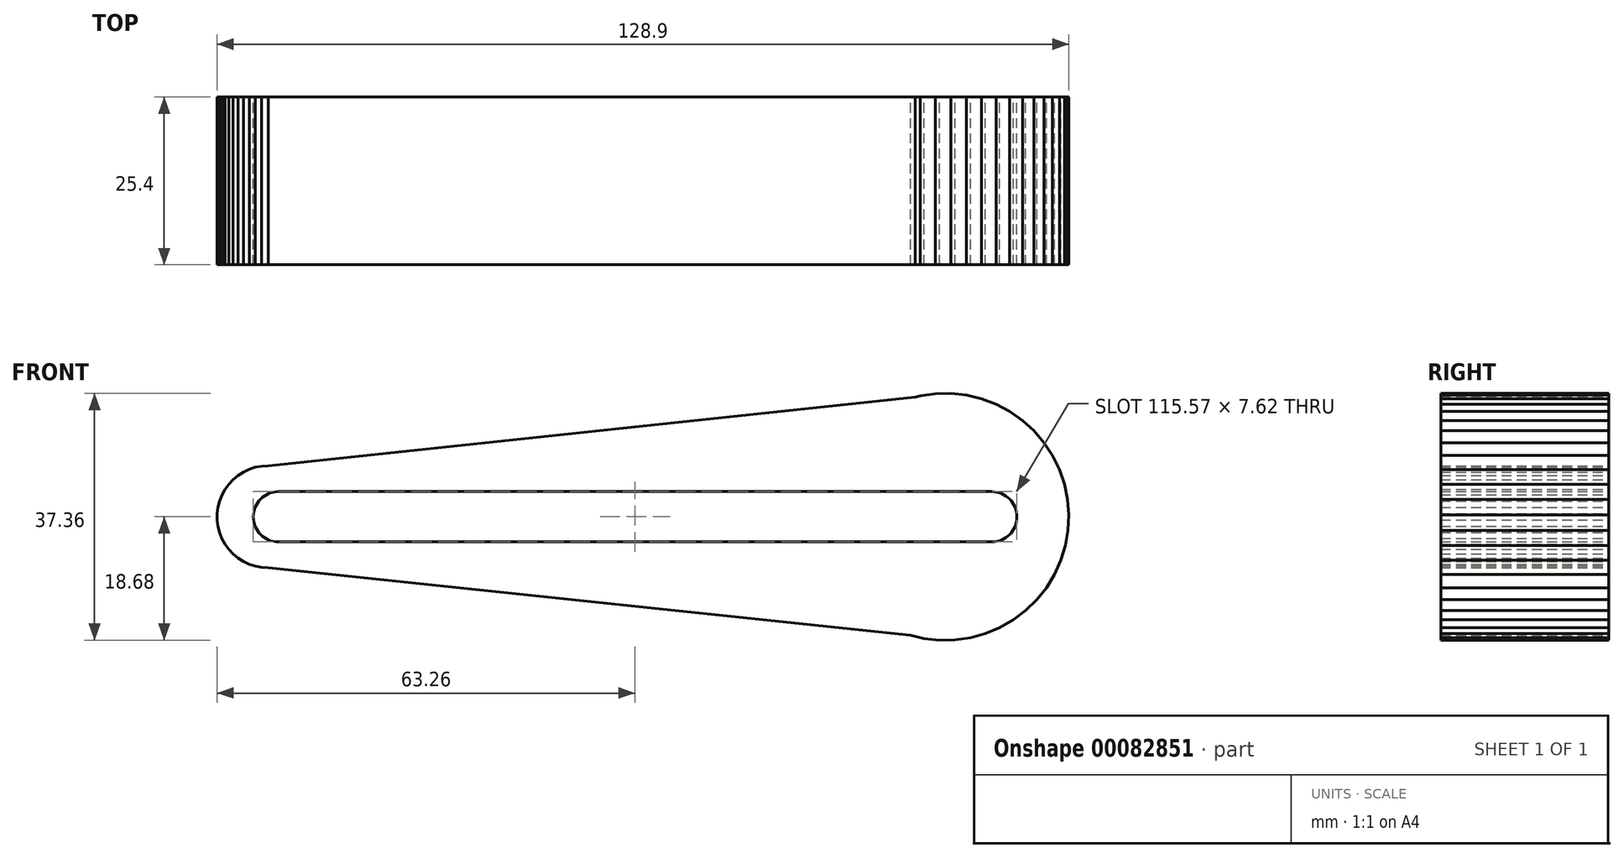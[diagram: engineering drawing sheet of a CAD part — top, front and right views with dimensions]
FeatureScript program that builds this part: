
annotation { "Feature Type Name" : "Feature", "Feature Type Description" : "" }
export const myFeature = defineFeature(function(context is Context, id is Id, definition is map)
    precondition{}
    {
        {
            var Q0;
            Q0=qCreatedBy(makeId("Front.planeOp"),FACE);
            var sketch = newSketch(context, id + "F0", { "sketchPlane" : qUnion([Q0])});
            skCircle(sketch, "E0.cCircle", {"center": v(46.95, 0) * mm, "radius": 18.66 * mm, "construction": true});
            skLineSegment(sketch, "E0.0", {"start": v(36.67, 15.62) * mm, "end": v(38.7, 16.78) * mm});
            skLineSegment(sketch, "E0.1", {"start": v(38.7, 16.78) * mm, "end": v(40.88, 17.68) * mm});
            skLineSegment(sketch, "E0.2", {"start": v(40.88, 17.68) * mm, "end": v(43.14, 18.3) * mm});
            skLineSegment(sketch, "E0.3", {"start": v(43.14, 18.3) * mm, "end": v(45.47, 18.64) * mm});
            skLineSegment(sketch, "E0.4", {"start": v(45.47, 18.64) * mm, "end": v(47.81, 18.68) * mm});
            skLineSegment(sketch, "E0.5", {"start": v(47.81, 18.68) * mm, "end": v(50.15, 18.42) * mm});
            skLineSegment(sketch, "E0.6", {"start": v(50.15, 18.42) * mm, "end": v(52.43, 17.87) * mm});
            skLineSegment(sketch, "E0.7", {"start": v(52.43, 17.87) * mm, "end": v(54.63, 17.05) * mm});
            skLineSegment(sketch, "E0.8", {"start": v(54.63, 17.05) * mm, "end": v(56.7, 15.95) * mm});
            skLineSegment(sketch, "E0.9", {"start": v(56.7, 15.95) * mm, "end": v(58.63, 14.6) * mm});
            skLineSegment(sketch, "E0.10", {"start": v(58.63, 14.6) * mm, "end": v(60.36, 13.02) * mm});
            skLineSegment(sketch, "E0.11", {"start": v(60.36, 13.02) * mm, "end": v(61.89, 11.24) * mm});
            skLineSegment(sketch, "E0.12", {"start": v(61.89, 11.24) * mm, "end": v(63.18, 9.28) * mm});
            skLineSegment(sketch, "E0.13", {"start": v(63.18, 9.28) * mm, "end": v(64.21, 7.17) * mm});
            skLineSegment(sketch, "E0.14", {"start": v(64.21, 7.17) * mm, "end": v(64.98, 4.95) * mm});
            skLineSegment(sketch, "E0.15", {"start": v(64.98, 4.95) * mm, "end": v(65.46, 2.65) * mm});
            skLineSegment(sketch, "E0.16", {"start": v(65.46, 2.65) * mm, "end": v(65.64, 0.3) * mm});
            skLineSegment(sketch, "E0.17", {"start": v(65.64, 0.3) * mm, "end": v(65.53, -2.04) * mm});
            skLineSegment(sketch, "E0.18", {"start": v(65.53, -2.04) * mm, "end": v(65.13, -4.35) * mm});
            skLineSegment(sketch, "E0.19", {"start": v(65.13, -4.35) * mm, "end": v(64.44, -6.6) * mm});
            skLineSegment(sketch, "E0.20", {"start": v(64.44, -6.6) * mm, "end": v(63.48, -8.74) * mm});
            skLineSegment(sketch, "E0.21", {"start": v(63.48, -8.74) * mm, "end": v(62.25, -10.74) * mm});
            skLineSegment(sketch, "E0.22", {"start": v(62.25, -10.74) * mm, "end": v(60.79, -12.57) * mm});
            skLineSegment(sketch, "E0.23", {"start": v(60.79, -12.57) * mm, "end": v(59.1, -14.2) * mm});
            skLineSegment(sketch, "E0.24", {"start": v(59.1, -14.2) * mm, "end": v(57.22, -15.62) * mm});
            skLineSegment(sketch, "E0.25", {"start": v(57.22, -15.62) * mm, "end": v(55.19, -16.78) * mm});
            skLineSegment(sketch, "E0.26", {"start": v(55.19, -16.78) * mm, "end": v(53.02, -17.68) * mm});
            skLineSegment(sketch, "E0.27", {"start": v(53.02, -17.68) * mm, "end": v(50.75, -18.3) * mm});
            skLineSegment(sketch, "E0.28", {"start": v(50.75, -18.3) * mm, "end": v(48.43, -18.64) * mm});
            skLineSegment(sketch, "E0.29", {"start": v(48.43, -18.64) * mm, "end": v(46.08, -18.68) * mm});
            skLineSegment(sketch, "E0.30", {"start": v(46.08, -18.68) * mm, "end": v(43.75, -18.42) * mm});
            skLineSegment(sketch, "E0.31", {"start": v(43.75, -18.42) * mm, "end": v(41.46, -17.87) * mm});
            skLineSegment(sketch, "E0.32", {"start": v(41.46, -17.87) * mm, "end": v(39.27, -17.05) * mm});
            skLineSegment(sketch, "E0.33", {"start": v(39.27, -17.05) * mm, "end": v(37.2, -15.95) * mm});
            skLineSegment(sketch, "E0.34", {"start": v(37.2, -15.95) * mm, "end": v(35.27, -14.6) * mm});
            skLineSegment(sketch, "E0.35", {"start": v(35.27, -14.6) * mm, "end": v(33.53, -13.02) * mm});
            skLineSegment(sketch, "E0.36", {"start": v(33.53, -13.02) * mm, "end": v(32, -11.24) * mm});
            skLineSegment(sketch, "E0.37", {"start": v(32, -11.24) * mm, "end": v(30.72, -9.28) * mm});
            skLineSegment(sketch, "E0.38", {"start": v(30.72, -9.28) * mm, "end": v(29.68, -7.17) * mm});
            skLineSegment(sketch, "E0.39", {"start": v(29.68, -7.17) * mm, "end": v(28.92, -4.95) * mm});
            skLineSegment(sketch, "E0.40", {"start": v(28.92, -4.95) * mm, "end": v(28.44, -2.65) * mm});
            skLineSegment(sketch, "E0.41", {"start": v(28.44, -2.65) * mm, "end": v(28.25, -0.3) * mm});
            skLineSegment(sketch, "E0.42", {"start": v(28.25, -0.3) * mm, "end": v(28.36, 2.04) * mm});
            skLineSegment(sketch, "E0.43", {"start": v(28.36, 2.04) * mm, "end": v(28.77, 4.35) * mm});
            skLineSegment(sketch, "E0.44", {"start": v(28.77, 4.35) * mm, "end": v(29.45, 6.6) * mm});
            skLineSegment(sketch, "E0.45", {"start": v(29.45, 6.6) * mm, "end": v(30.42, 8.74) * mm});
            skLineSegment(sketch, "E0.46", {"start": v(30.42, 8.74) * mm, "end": v(31.64, 10.74) * mm});
            skLineSegment(sketch, "E0.47", {"start": v(31.64, 10.74) * mm, "end": v(33.11, 12.57) * mm});
            skLineSegment(sketch, "E0.48", {"start": v(33.11, 12.57) * mm, "end": v(34.8, 14.2) * mm});
            skLineSegment(sketch, "E0.49", {"start": v(34.8, 14.2) * mm, "end": v(36.67, 15.62) * mm});
            skPoint(sketch, "E0.0.midPoint", {"position": v(37.7, 16.2) * mm});
            skCircle(sketch, "E1.cCircle", {"center": v(-55.54, 0) * mm, "radius": 7.72 * mm, "construction": true});
            skLineSegment(sketch, "E1.0", {"start": v(-61.5, 4.94) * mm, "end": v(-60.83, 5.64) * mm});
            skLineSegment(sketch, "E1.1", {"start": v(-60.83, 5.64) * mm, "end": v(-60.08, 6.26) * mm});
            skLineSegment(sketch, "E1.2", {"start": v(-60.08, 6.26) * mm, "end": v(-59.26, 6.78) * mm});
            skLineSegment(sketch, "E1.3", {"start": v(-59.26, 6.78) * mm, "end": v(-58.38, 7.2) * mm});
            skLineSegment(sketch, "E1.4", {"start": v(-58.38, 7.2) * mm, "end": v(-57.46, 7.5) * mm});
            skLineSegment(sketch, "E1.5", {"start": v(-57.46, 7.5) * mm, "end": v(-56.5, 7.67) * mm});
            skLineSegment(sketch, "E1.6", {"start": v(-56.5, 7.67) * mm, "end": v(-55.54, 7.73) * mm});
            skLineSegment(sketch, "E1.7", {"start": v(-55.54, 7.73) * mm, "end": v(-54.57, 7.67) * mm});
            skLineSegment(sketch, "E1.8", {"start": v(-54.57, 7.67) * mm, "end": v(-53.61, 7.49) * mm});
            skLineSegment(sketch, "E1.9", {"start": v(-53.61, 7.49) * mm, "end": v(-52.69, 7.19) * mm});
            skLineSegment(sketch, "E1.10", {"start": v(-52.69, 7.19) * mm, "end": v(-51.81, 6.77) * mm});
            skLineSegment(sketch, "E1.11", {"start": v(-51.81, 6.77) * mm, "end": v(-51, 6.25) * mm});
            skLineSegment(sketch, "E1.12", {"start": v(-51, 6.25) * mm, "end": v(-50.24, 5.63) * mm});
            skLineSegment(sketch, "E1.13", {"start": v(-50.24, 5.63) * mm, "end": v(-49.58, 4.92) * mm});
            skLineSegment(sketch, "E1.14", {"start": v(-49.58, 4.92) * mm, "end": v(-49, 4.14) * mm});
            skLineSegment(sketch, "E1.15", {"start": v(-49, 4.14) * mm, "end": v(-48.54, 3.28) * mm});
            skLineSegment(sketch, "E1.16", {"start": v(-48.54, 3.28) * mm, "end": v(-48.19, 2.38) * mm});
            skLineSegment(sketch, "E1.17", {"start": v(-48.19, 2.38) * mm, "end": v(-47.95, 1.44) * mm});
            skLineSegment(sketch, "E1.18", {"start": v(-47.95, 1.44) * mm, "end": v(-47.83, 0.48) * mm});
            skLineSegment(sketch, "E1.19", {"start": v(-47.83, 0.48) * mm, "end": v(-47.83, -0.5) * mm});
            skLineSegment(sketch, "E1.20", {"start": v(-47.83, -0.5) * mm, "end": v(-47.95, -1.46) * mm});
            skLineSegment(sketch, "E1.21", {"start": v(-47.95, -1.46) * mm, "end": v(-48.2, -2.4) * mm});
            skLineSegment(sketch, "E1.22", {"start": v(-48.2, -2.4) * mm, "end": v(-48.55, -3.3) * mm});
            skLineSegment(sketch, "E1.23", {"start": v(-48.55, -3.3) * mm, "end": v(-49.02, -4.15) * mm});
            skLineSegment(sketch, "E1.24", {"start": v(-49.02, -4.15) * mm, "end": v(-49.6, -4.94) * mm});
            skLineSegment(sketch, "E1.25", {"start": v(-49.6, -4.94) * mm, "end": v(-50.26, -5.64) * mm});
            skLineSegment(sketch, "E1.26", {"start": v(-50.26, -5.64) * mm, "end": v(-51, -6.26) * mm});
            skLineSegment(sketch, "E1.27", {"start": v(-51, -6.26) * mm, "end": v(-51.83, -6.78) * mm});
            skLineSegment(sketch, "E1.28", {"start": v(-51.83, -6.78) * mm, "end": v(-52.7, -7.2) * mm});
            skLineSegment(sketch, "E1.29", {"start": v(-52.7, -7.2) * mm, "end": v(-53.63, -7.5) * mm});
            skLineSegment(sketch, "E1.30", {"start": v(-53.63, -7.5) * mm, "end": v(-54.58, -7.67) * mm});
            skLineSegment(sketch, "E1.31", {"start": v(-54.58, -7.67) * mm, "end": v(-55.55, -7.73) * mm});
            skLineSegment(sketch, "E1.32", {"start": v(-55.55, -7.73) * mm, "end": v(-56.52, -7.67) * mm});
            skLineSegment(sketch, "E1.33", {"start": v(-56.52, -7.67) * mm, "end": v(-57.48, -7.49) * mm});
            skLineSegment(sketch, "E1.34", {"start": v(-57.48, -7.49) * mm, "end": v(-58.4, -7.19) * mm});
            skLineSegment(sketch, "E1.35", {"start": v(-58.4, -7.19) * mm, "end": v(-59.28, -6.77) * mm});
            skLineSegment(sketch, "E1.36", {"start": v(-59.28, -6.77) * mm, "end": v(-60.1, -6.25) * mm});
            skLineSegment(sketch, "E1.37", {"start": v(-60.1, -6.25) * mm, "end": v(-60.84, -5.63) * mm});
            skLineSegment(sketch, "E1.38", {"start": v(-60.84, -5.63) * mm, "end": v(-61.5, -4.92) * mm});
            skLineSegment(sketch, "E1.39", {"start": v(-61.5, -4.92) * mm, "end": v(-62.08, -4.14) * mm});
            skLineSegment(sketch, "E1.40", {"start": v(-62.08, -4.14) * mm, "end": v(-62.55, -3.28) * mm});
            skLineSegment(sketch, "E1.41", {"start": v(-62.55, -3.28) * mm, "end": v(-62.9, -2.38) * mm});
            skLineSegment(sketch, "E1.42", {"start": v(-62.9, -2.38) * mm, "end": v(-63.14, -1.44) * mm});
            skLineSegment(sketch, "E1.43", {"start": v(-63.14, -1.44) * mm, "end": v(-63.26, -0.48) * mm});
            skLineSegment(sketch, "E1.44", {"start": v(-63.26, -0.48) * mm, "end": v(-63.26, 0.5) * mm});
            skLineSegment(sketch, "E1.45", {"start": v(-63.26, 0.5) * mm, "end": v(-63.14, 1.46) * mm});
            skLineSegment(sketch, "E1.46", {"start": v(-63.14, 1.46) * mm, "end": v(-62.9, 2.4) * mm});
            skLineSegment(sketch, "E1.47", {"start": v(-62.9, 2.4) * mm, "end": v(-62.54, 3.3) * mm});
            skLineSegment(sketch, "E1.48", {"start": v(-62.54, 3.3) * mm, "end": v(-62.07, 4.15) * mm});
            skLineSegment(sketch, "E1.49", {"start": v(-62.07, 4.15) * mm, "end": v(-61.5, 4.94) * mm});
            skPoint(sketch, "E1.0.midPoint", {"position": v(-61.16, 5.29) * mm});
            skLineSegment(sketch, "E2", {"start": v(-55.54, 7.73) * mm, "end": v(47.81, 18.68) * mm});
            skLineSegment(sketch, "E3", {"start": v(-55.55, -7.73) * mm, "end": v(48.43, -18.64) * mm});
            skSolve(sketch);
        }
        {
            var Q0;
            Q0 = qSketchRegion(id + "F0", true);
            extrude(context, id + "F1", {"entities" : qUnion([Q0]), "depth" : 25.4 * mm});
        }
        {
            var Q0;
            Q0=qCreatedBy(makeId("Front.planeOp"),FACE);
            var sketch = newSketch(context, id + "F2", { "sketchPlane" : qUnion([Q0])});
            skLineSegment(sketch, "E4.bottom", {"start": v(-53.98, 3.8) * mm, "end": v(53.98, 3.8) * mm});
            skLineSegment(sketch, "E4.top", {"start": v(-53.98, -3.81) * mm, "end": v(53.98, -3.81) * mm});
            skLineSegment(sketch, "E4.left", {"start": v(-53.98, 3.8) * mm, "end": v(-53.98, -3.8) * mm});
            skLineSegment(sketch, "E4.right", {"start": v(53.98, 3.8) * mm, "end": v(53.98, -3.8) * mm});
            skPoint(sketch, "E4.middle", {"position": v(0, 0) * mm});
            skArc(sketch, "E5", {"start": v(-53.98, 3.81) * mm, "mid": v(-57.79, 0) * mm, "end": v(-53.98, -3.81) * mm});
            skArc(sketch, "E6", {"start": v(53.98, -3.8) * mm, "mid": v(57.79, 0) * mm, "end": v(53.98, 3.8) * mm});
            skSolve(sketch);
        }
        {
            var Q0;
            Q0 = qSketchRegion(id + "F2", true);
            extrude(context, id + "F3", {"entities" : qUnion([Q0]), "operationType" : NewBodyOperationType.REMOVE, "depth" : 25.4 * mm});
        }
    });
